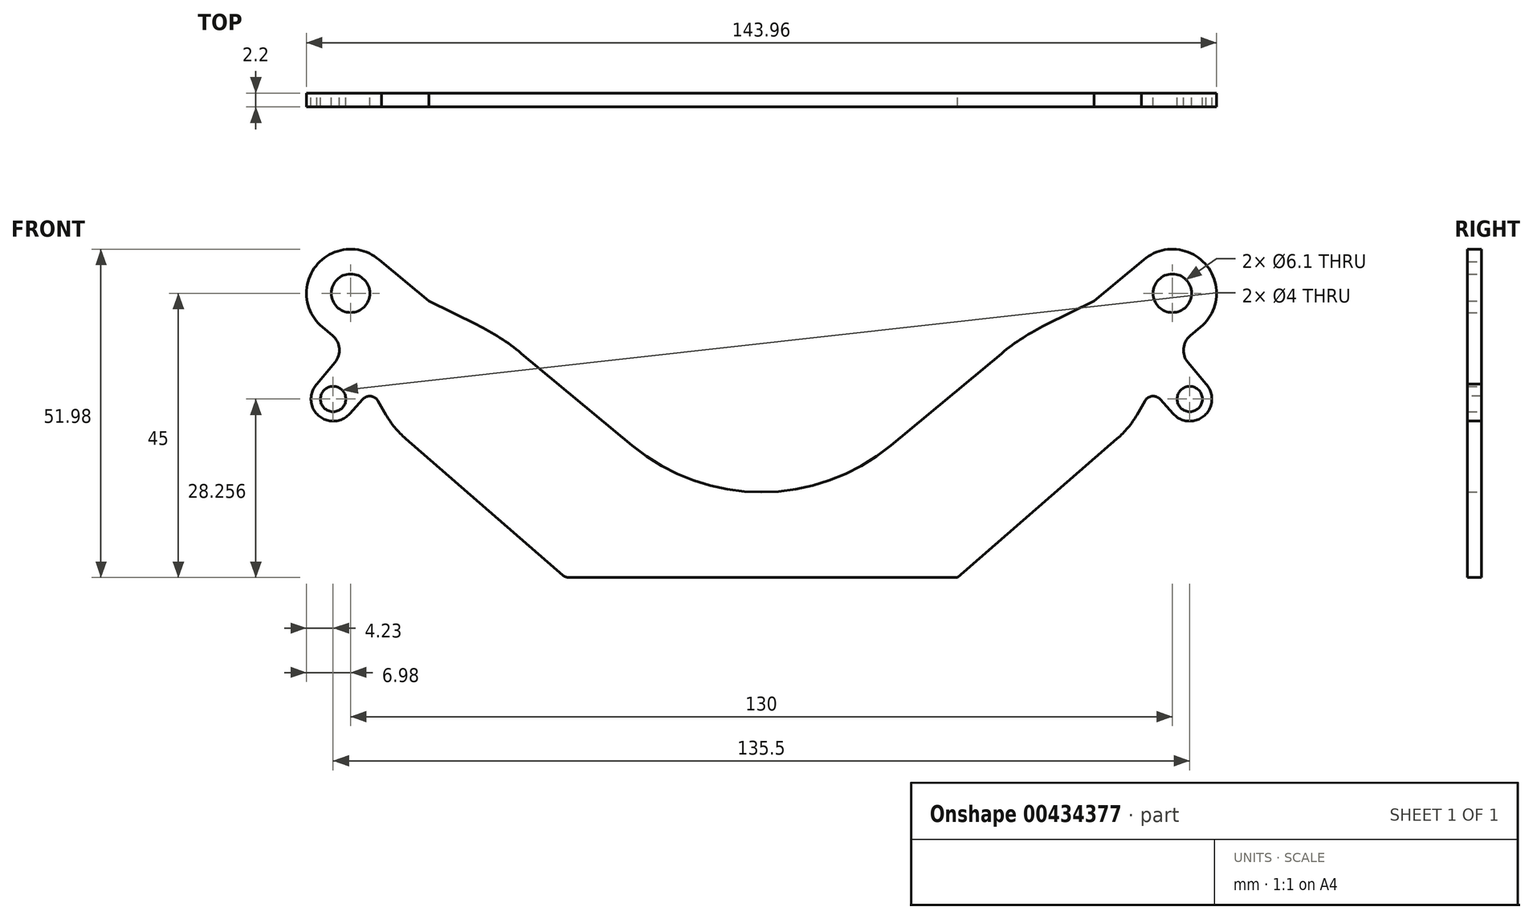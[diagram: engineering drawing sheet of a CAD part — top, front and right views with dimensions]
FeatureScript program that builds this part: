
annotation { "Feature Type Name" : "Feature", "Feature Type Description" : "" }
export const myFeature = defineFeature(function(context is Context, id is Id, definition is map)
    precondition{}
    {
        {
            var Q0;
            Q0=qCreatedBy(makeId("Front.planeOp"),FACE);
            var sketch = newSketch(context, id + "F0", { "sketchPlane" : qUnion([Q0])});
            skLineSegment(sketch, "E0", {"start": v(65, 87) * mm, "end": v(47.82, 87) * mm, "construction": true});
            skCircle(sketch, "E1", {"center": v(65, 132) * mm, "radius": 3.05 * mm});
            skLineSegment(sketch, "E2", {"start": v(0, -44.96) * mm, "end": v(0, 184.97) * mm, "construction": true});
            skLineSegment(sketch, "E3.0", {"start": v(41.21, 125.17) * mm, "end": v(20.46, 107.91) * mm});
            skPoint(sketch, "E4.orphan", {"position": v(0, 92) * mm});
            skPoint(sketch, "E5.orphan", {"position": v(31, 87) * mm});
            skLineSegment(sketch, "E6.trimOffspring", {"start": v(61.53, 87) * mm, "end": v(65, 87) * mm, "construction": true});
            skLineSegment(sketch, "E7", {"start": v(65, 132) * mm, "end": v(65, 163.8) * mm, "construction": true});
            skLineSegment(sketch, "E8", {"start": v(65, 132) * mm, "end": v(70.87, 140.45) * mm, "construction": true});
            skArc(sketch, "E9", {"start": v(69.46, 126.63) * mm, "mid": v(70.18, 136.68) * mm, "end": v(60.1, 136.98) * mm});
            skLineSegment(sketch, "E10", {"start": v(60.1, 136.98) * mm, "end": v(52.62, 130.75) * mm});
            skLineSegment(sketch, "E11", {"start": v(52.62, 130.75) * mm, "end": v(41.21, 125.17) * mm});
            skLineSegment(sketch, "E12", {"start": v(69.46, 126.63) * mm, "end": v(65.54, 123.38) * mm});
            skLineSegment(sketch, "E13", {"start": v(65, 132) * mm, "end": v(10.88, 87) * mm, "construction": true});
            skCircle(sketch, "E14", {"center": v(67.75, 115.26) * mm, "radius": 2 * mm});
            skArc(sketch, "E15", {"start": v(65.15, 112.92) * mm, "mid": v(70.12, 112.68) * mm, "end": v(70.3, 117.65) * mm});
            skLineSegment(sketch, "E16", {"start": v(70.3, 117.65) * mm, "end": v(65.54, 123.38) * mm});
            skLineSegment(sketch, "E17", {"start": v(65.15, 112.92) * mm, "end": v(61.7, 116.75) * mm});
            skLineSegment(sketch, "E18", {"start": v(67.75, 115.26) * mm, "end": v(58.4, 126.5) * mm, "construction": true});
            skLineSegment(sketch, "E19.trimOffspring", {"start": v(61.7, 116.75) * mm, "end": v(58.15, 110.6) * mm});
            skLineSegment(sketch, "E20", {"start": v(58.15, 110.6) * mm, "end": v(31, 87) * mm});
            skCircle(sketch, "E21.MirrorC", {"center": v(-65, 132) * mm, "radius": 3.05 * mm});
            skLineSegment(sketch, "E22.MirrorCS", {"start": v(-65, 132) * mm, "end": v(-70.87, 140.45) * mm, "construction": true});
            skArc(sketch, "E23.MirrorCS", {"start": v(-65.15, 112.92) * mm, "mid": v(-70.12, 112.68) * mm, "end": v(-70.3, 117.65) * mm});
            skLineSegment(sketch, "E24.MirrorCS", {"start": v(-65.15, 112.92) * mm, "end": v(-61.7, 116.75) * mm});
            skLineSegment(sketch, "E25.MirrorCS", {"start": v(-70.3, 117.65) * mm, "end": v(-65.54, 123.38) * mm});
            skCircle(sketch, "E26.MirrorC", {"center": v(-67.75, 115.26) * mm, "radius": 2 * mm});
            skLineSegment(sketch, "E27.MirrorCS", {"start": v(-67.75, 115.26) * mm, "end": v(-58.4, 126.5) * mm, "construction": true});
            skLineSegment(sketch, "E28.MirrorCS", {"start": v(-60.1, 136.98) * mm, "end": v(-52.62, 130.75) * mm});
            skLineSegment(sketch, "E29.MirrorCS", {"start": v(-61.7, 116.75) * mm, "end": v(-58.15, 110.6) * mm});
            skLineSegment(sketch, "E30.MirrorCS", {"start": v(-52.62, 130.75) * mm, "end": v(-41.21, 125.17) * mm});
            skLineSegment(sketch, "E31.MirrorCS", {"start": v(-69.46, 126.63) * mm, "end": v(-65.54, 123.38) * mm});
            skArc(sketch, "E32.MirrorCS", {"start": v(-69.46, 126.63) * mm, "mid": v(-70.18, 136.68) * mm, "end": v(-60.1, 136.98) * mm});
            skLineSegment(sketch, "E33.MirrorCS", {"start": v(-65, 87) * mm, "end": v(-47.82, 87) * mm, "construction": true});
            skLineSegment(sketch, "E34.MirrorCS", {"start": v(-61.53, 87) * mm, "end": v(-65, 87) * mm, "construction": true});
            skPoint(sketch, "E35.MirrorP", {"position": v(-31, 87) * mm});
            skLineSegment(sketch, "E36.MirrorCS", {"start": v(-58.15, 110.6) * mm, "end": v(-31, 87) * mm});
            skLineSegment(sketch, "E37.MirrorCS", {"start": v(-65, 132) * mm, "end": v(-10.88, 87) * mm, "construction": true});
            skLineSegment(sketch, "E38.MirrorCS", {"start": v(-65, 132) * mm, "end": v(-65, 163.8) * mm, "construction": true});
            skLineSegment(sketch, "E39.MirrorCS", {"start": v(-41.21, 125.17) * mm, "end": v(-20.46, 107.91) * mm});
            skLineSegment(sketch, "E40", {"start": v(-47.82, 87) * mm, "end": v(47.82, 87) * mm, "construction": true});
            skLineSegment(sketch, "E41", {"start": v(31, 87) * mm, "end": v(-31, 87) * mm});
            skPoint(sketch, "E42.visualSharp", {"position": v(0, 90.9) * mm});
            skArc(sketch, "E42.filletArc", {"start": v(-20.46, 107.91) * mm, "mid": v(0, 100.52) * mm, "end": v(20.46, 107.91) * mm});
            skSolve(sketch);
        }
        {
            var Q0;
            Q0=qSketchRegion(id+"F0",true);
            extrude(context, id + "F1", {"entities" : qUnion([Q0]), "depth" : 2.2 * mm});
        }
        {
            var Q0;
            Q0=makeQuery(id+"F1.opExtrude","SWEPT_EDGE",EDGE,{"disambiguationData":[OSD([sQuery(id+"F0.wireOp",EDGE,"E3.0"),sQuery(id+"F0.wireOp",EDGE,"E39.MirrorCS")])]});
            fillet(context, id + "F2", {"entities" : qUnion([Q0]), "radius" : 35 * mm, "tangentPropagation" : true, "allowEdgeOverflow" : false});
        }
        {
            var Q0;
            Q0=makeQuery(id+"F1.opExtrude","SWEPT_EDGE",EDGE,{"disambiguationData":[OSD([sQuery(id+"F0.wireOp",EDGE,"E19.trimOffspring"),sQuery(id+"F0.wireOp",EDGE,"E20")])]});
            var Q1;
            Q1=makeQuery(id+"F1.opExtrude","SWEPT_EDGE",EDGE,{"disambiguationData":[OSD([sQuery(id+"F0.wireOp",EDGE,"E29.MirrorCS"),sQuery(id+"F0.wireOp",EDGE,"E36.MirrorCS")])]});
            fillet(context, id + "F3", {"entities" : qUnion([Q0, Q1]), "radius" : 15 * mm, "tangentPropagation" : true, "allowEdgeOverflow" : false});
        }
        {
            var Q0;
            Q0=makeQuery(id+"F1.opExtrude","SWEPT_EDGE",EDGE,{"disambiguationData":[OSD([sQuery(id+"F0.wireOp",EDGE,"E36.MirrorCS"),sQuery(id+"F0.wireOp",EDGE,"0aebadc9-47d1-4a55-8ed3-6b3125491064.trimOffspring")])]});
            var Q1;
            Q1=makeQuery(id+"F1.opExtrude","SWEPT_EDGE",EDGE,{"disambiguationData":[OSD([sQuery(id+"F0.wireOp",EDGE,"E24.MirrorCS"),sQuery(id+"F0.wireOp",EDGE,"E29.MirrorCS")])]});
            var Q2;
            Q2=makeQuery(id+"F1.opExtrude","SWEPT_EDGE",EDGE,{"disambiguationData":[OSD([sQuery(id+"F0.wireOp",EDGE,"E17"),sQuery(id+"F0.wireOp",EDGE,"E19.trimOffspring")])]});
            fillet(context, id + "F4", {"entities" : qUnion([Q0, Q1, Q2]), "radius" : 1.5 * mm, "tangentPropagation" : true, "allowEdgeOverflow" : false});
        }
        {
            var Q0;
            Q0=makeQuery(id+"F1.opExtrude","SWEPT_EDGE",EDGE,{"disambiguationData":[OSD([sQuery(id+"F0.wireOp",EDGE,"E12"),sQuery(id+"F0.wireOp",EDGE,"E16")])]});
            var Q1;
            Q1=makeQuery(id+"F1.opExtrude","SWEPT_EDGE",EDGE,{"disambiguationData":[OSD([sQuery(id+"F0.wireOp",EDGE,"E25.MirrorCS"),sQuery(id+"F0.wireOp",EDGE,"E31.MirrorCS")])]});
            fillet(context, id + "F5", {"entities" : qUnion([Q0, Q1]), "radius" : 3 * mm, "tangentPropagation" : true, "allowEdgeOverflow" : false});
        }
    });
